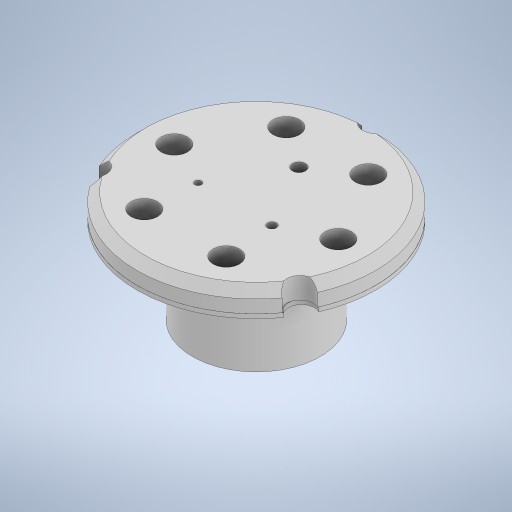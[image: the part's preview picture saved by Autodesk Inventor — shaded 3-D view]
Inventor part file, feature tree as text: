
AUTODESK INVENTOR PART (.ipt)
format: ipt  version: 2023.2 (Build 272271030, 271C)  size: 390,144 bytes
history: native  units: mm
features: sketch x7, hole x4, extrude x3, chamfer x2
ambient origin geometry x8: Origin, YZ Plane, XZ Plane, XY Plane, X Axis, Y Axis, Z Axis, Center Point
bodies: Solid1 (feature_tree)
feature tree (16):
  extrude  "Extrusion1"  Depth=20.0mm TaperAngle=0.0deg
  extrude  "Extrusion2"  Depth=1.0mm TaperAngle=0.0deg
  chamfer  "Chamfer1"  Distance=0.01mm Angle=45.0deg
  extrude  "Extrusion3"  Depth=60.0mm TaperAngle=360.0deg
  hole  "Hole1"  [1 undecoded]
  hole  "Hole2"  [1 undecoded]
  hole  "Hole3"  [1 undecoded]
  hole  "Hole4"  [1 undecoded]
  chamfer  "Chamfer2"  [1 undecoded]
  sketch  "Sketch1"  dims[d0=30.0mm d1=20.0mm d2=0.0mm]
  sketch  "Sketch2"  dims[d3=56.0mm d4=1.0mm d5=0.0mm d6=0.01mm d7=2.0mm d8=45.0deg]
  sketch  "Sketch3"  dims[d9=6.2mm d11=60.0mm d13=360.0deg]
  sketch  "Sketch4"  dims[d15=6.1mm d16=30.0mm d18=360.0deg]
  sketch  "Sketch5"  dims[d21=3.1mm d22=2.1mm]
  sketch  "Sketch6"  dims[d23=1.6mm d24=5.0mm d25=0.0mm]
  sketch  "Sketch7"  dims[d26=6.2mm d27=6.0mm d28=4.0mm d29=2.0mm d30=90.0deg d31=8.0mm d32=20.594885mm d33=2.1mm d34=6.0mm d35=4.0mm d36=2.0mm d37=90.0deg d38=8.0mm d39=20.594885mm d40=6.1mm d41=6.0mm d42=4.0mm d43=2.0mm d44=90.0deg d45=8.0mm d46=20.594885mm d47=6.1mm d48=6.0mm d49=4.0mm d50=2.0mm d51=90.0deg d52=8.0mm d53=20.594885mm d54=2.0mm d55=2.0mm d56=45.0deg]
note: 5 required parameter values undecoded (feature->parameter linkage not recoverable at this tier; creation-order binding heuristic only, values carry confidence <= 0.55)
